# Revit family: LAMP_KOMBIC 150 SURFACE 3000 CRI80 OPTIC DALI
name_source: partatom
category: Luminarias
revit_build: Autodesk Revit 2018 (Build: 20190510_1515(x64)
units: mm (PartAtom-declared; Revit-internal decimal feet)

## family parameters
Anfitrión = Cara
Compartido = No
Corte con vacíos al cargar = No
Cota de conector redondo = Diámetro de uso
Origen de luz = Sí
Punto de cálculo de habitación = No
Tipo de pieza = Normal

## types (12) — shared parameters
CRI = 80
Cambio de temperatura de color de luz atenuada = <Ninguno>
Diameter = 150 mm
Elevación por defecto = 1219 mm
Fabricante = LAMP
Filtro de color = 16777215
Gear = Adjustable DALI
Height = 180 mm  [stored 0.590551 ft]
IEE = A+
Installation instructions = https://www.lamp.es
Insulation class = II
LED Lifetime = 50.000 L80 B10
Lamp = COB LED
Last update = 07/10/2021
Luminaire type = Suspended
MacAdam = 3
Manufacturer URL = http://www.lamp.es
Manufacturer country = Spain
Manufacturer name = LAMP
Material cable suspension = LAMP_Acero genérico
Material difusor = LAMP_PMMA Difusor Kombic
Model explanation = Possibility of chossing between surface or suspended within the model
Plum = 20 W
Power = 18 W
Power Supply = 220-240V 50/60Hz
Product URL = https://www.lamp.es
Product datasheet = http://www.lamp.es
Protection rating = IP40
Type = COB PHILIPS
UGR = 19
Weight = 1.74 kg
Ángulo de inclinación = -90.00°

## per-type parameters (varying)
| type | Archivo de red fotométrica | Efficacy | Finish | Material cuerpo | Material floron | Material reflector | Modelo | Product code |
| 1613LM 3000K  B/B | K21SF3040WF830NBB.IES | 82 lm/W | Matte black RAL 9011 | LAMP_Plástico genérico NG | LAMP_Plástico genérico NG | LAMP_PC Reflector Kombic Metalizado Negro | K21SF3040WF830DBB | K21SF3040WF830DBB |
| 1613LM 3000K  B/W | K21SF3040WF830NBW.IES | 82 lm/W | Matte white RAL 9010 | LAMP_Plástico genérico BL | LAMP_Plástico genérico BL | LAMP_PC Reflector Kombic Metalizado Negro | K21SF3040WF830DBW | K21SF3040WF830DBW |
| 1618LM 3000K  M/B | K21SF3040WF830NMB.IES | 82 lm/W | Matte black RAL 9011 | LAMP_Plástico genérico NG | LAMP_Plástico genérico NG | LAMP_PC Reflector Kombic Metalizado Mate | K21SF3040WF830DMB | K21SF3040WF830DMB |
| 1618LM 3000K  M/W | K21SF3040WF830NMW.IES | 82 lm/W | Matte white RAL 9010 | LAMP_Plástico genérico BL | LAMP_Plástico genérico BL | LAMP_PC Reflector Kombic Metalizado Mate | K21SF3040WF830DMW | K21SF3040WF830DMW |
| 1667LM 3000K  W/B | K21SF3040WF830NWB.IES | 84 lm/W | Matte black RAL 9011 | LAMP_Plástico genérico NG | LAMP_Plástico genérico NG | LAMP_PC Reflector Kombic Blanco | K21SF3040WF830DWB | K21SF3040WF830DWB |
| 1667LM 3000K  W/W | K21SF3040WF830NWW.IES | 84 lm/W | Matte white RAL 9010 | LAMP_Plástico genérico BL | LAMP_Plástico genérico BL | LAMP_PC Reflector Kombic Blanco | K21SF3040WF830DWW | K21SF3040WF830DWW |
| 1680LM 4000K  B/B | K21SF3040WF840NBB.IES | 85 lm/W | Matte black RAL 9011 | LAMP_Plástico genérico NG | LAMP_Plástico genérico NG | LAMP_PC Reflector Kombic Metalizado Negro | K21SF3040WF840DBB | K21SF3040WF840DBB |
| 1680LM 4000K  B/W | K21SF3040WF840NBW.IES | 85 lm/W | Matte white RAL 9010 | LAMP_Plástico genérico BL | LAMP_Plástico genérico BL | LAMP_PC Reflector Kombic Metalizado Negro | K21SF3040WF840DBW | K21SF3040WF840DBW |
| 1685LM 4000K  M/B | K21SF3040WF840NMB.IES | 85 lm/W | Matte black RAL 9011 | LAMP_Plástico genérico NG | LAMP_Plástico genérico NG | LAMP_PC Reflector Kombic Metalizado Mate | K21SF3040WF840DMB | K21SF3040WF840DMB |
| 1685LM 4000K  M/W | K21SF3040WF840NMW.IES | 85 lm/W | Matte white RAL 9010 | LAMP_Plástico genérico BL | LAMP_Plástico genérico BL | LAMP_PC Reflector Kombic Metalizado Mate | K21SF3040WF840DMW | K21SF3040WF840DMW |
| 1737LM 4000K  W/B | K21SF3040WF840NWB.IES | 88 lm/W | Matte black RAL 9011 | LAMP_Plástico genérico NG | LAMP_Plástico genérico NG | LAMP_PC Reflector Kombic Blanco | K21SF3040WF840DWB | K21SF3040WF840DWB |
| 1737LM 4000K  W/W | K21SF3040WF840NWW.IES | 88 lm/W | Matte white RAL 9010 | LAMP_Plástico genérico BL | LAMP_Plástico genérico BL | LAMP_PC Reflector Kombic Blanco | K21SF3040WF840DWW | K21SF3040WF840DWW |

note: [stored X ft] marks values corroborated as IEEE doubles in the binary element streams (Revit-internal decimal feet)
